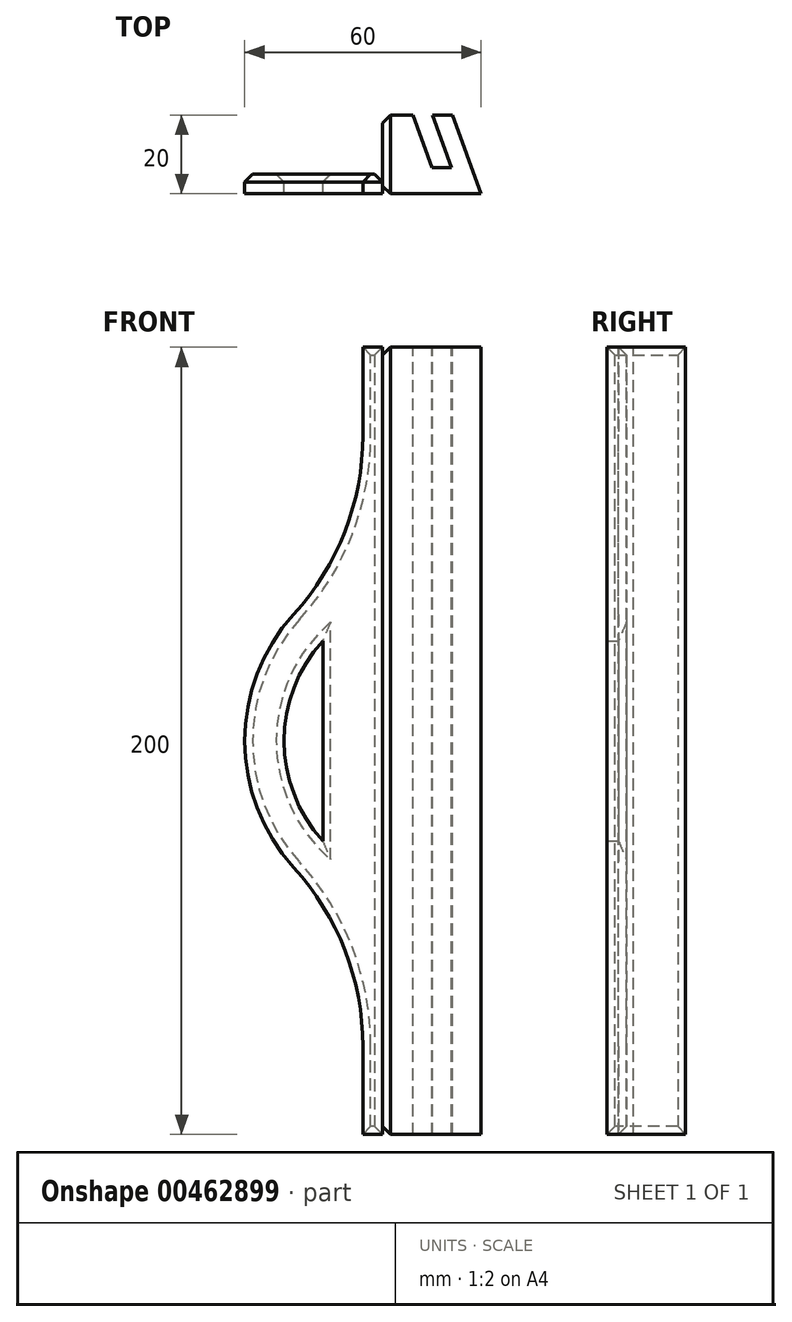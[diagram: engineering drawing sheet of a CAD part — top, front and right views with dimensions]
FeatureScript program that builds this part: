
annotation { "Feature Type Name" : "Feature", "Feature Type Description" : "" }
export const myFeature = defineFeature(function(context is Context, id is Id, definition is map)
    precondition{}
    {
        {
            var Q0;
            Q0=qCreatedBy(makeId("Top.planeOp"),FACE);
            var sketch = newSketch(context, id + "F0", { "sketchPlane" : qUnion([Q0])});
            skLineSegment(sketch, "E0", {"start": v(17.56, -12.97) * mm, "end": v(-7.44, -12.97) * mm});
            skLineSegment(sketch, "E1", {"start": v(-7.44, -12.97) * mm, "end": v(-0.16, 7.03) * mm});
            skLineSegment(sketch, "E2", {"start": v(-0.16, 7.03) * mm, "end": v(4.84, 7.03) * mm});
            skLineSegment(sketch, "E3", {"start": v(4.84, 7.03) * mm, "end": v(0, -6.27) * mm});
            skLineSegment(sketch, "E4", {"start": v(0, -6.27) * mm, "end": v(5, -6.27) * mm});
            skLineSegment(sketch, "E5", {"start": v(5, -6.27) * mm, "end": v(9.84, 7.03) * mm});
            skLineSegment(sketch, "E6", {"start": v(17.56, 7.03) * mm, "end": v(17.56, -12.97) * mm});
            skLineSegment(sketch, "E7", {"start": v(9.84, 7.03) * mm, "end": v(17.56, 7.03) * mm});
            skSolve(sketch);
        }
        {
            var Q0;
            Q0=qCreatedBy(makeId("Front.planeOp"),FACE);
            var sketch = newSketch(context, id + "F1", { "sketchPlane" : qUnion([Q0])});
            skLineSegment(sketch, "E8.left", {"start": v(0, 100) * mm, "end": v(0, 77.58) * mm});
            skArc(sketch, "E9", {"start": v(-17.57, 32.15) * mm, "mid": v(-30, 0) * mm, "end": v(-17.57, -32.15) * mm});
            skArc(sketch, "E10", {"start": v(0, -77.58) * mm, "mid": v(-4.54, -53.22) * mm, "end": v(-17.57, -32.15) * mm});
            skArc(sketch, "E11.trimOffspring", {"start": v(-17.57, 32.15) * mm, "mid": v(-4.54, 53.22) * mm, "end": v(0, 77.58) * mm});
            skArc(sketch, "E12.0", {"start": v(-10.17, 25.42) * mm, "mid": v(-20, 0) * mm, "end": v(-10.17, -25.42) * mm});
            skLineSegment(sketch, "E13", {"start": v(-10.17, 25.42) * mm, "end": v(-10.17, -25.42) * mm});
            skLineSegment(sketch, "E14", {"start": v(0, 100) * mm, "end": v(5, 100) * mm});
            skLineSegment(sketch, "E15", {"start": v(5, 100) * mm, "end": v(5, -100) * mm});
            skLineSegment(sketch, "E16", {"start": v(5, -100) * mm, "end": v(0, -100) * mm});
            skLineSegment(sketch, "E17.trimOffspring", {"start": v(0, -77.58) * mm, "end": v(0, -100) * mm});
            skSolve(sketch);
        }
        {
            var Q0;
            Q0=makeQuery(id+"F1.imprint","IMPRINT",FACE,{"disambiguationData":[TD([[makeQuery(id+"F1.imprint","IMPRINT",EDGE,{"derivedFrom":sQuery(id+"F1.wireOp",EDGE,"E8.left")}),1.0]])]});
            var Q1;
            Q1=sQuery(id+"F1.wireOp",EDGE,"E8.left");
            var Q2;
            Q2=sQuery(id+"F1.wireOp",EDGE,"E9");
            var Q3;
            Q3=sQuery(id+"F1.wireOp",EDGE,"E10");
            var Q4;
            Q4=sQuery(id+"F1.wireOp",EDGE,"E11.trimOffspring");
            var Q5;
            Q5=sQuery(id+"F1.wireOp",EDGE,"E15");
            var Q6;
            Q6=sQuery(id+"F1.wireOp",EDGE,"E17.trimOffspring");
            var Q7;
            Q7=sQuery(id+"F1.wireOp",EDGE,"E14");
            var Q8;
            Q8=sQuery(id+"F1.wireOp",EDGE,"E16");
            extrude(context, id + "F2", {"entities" : qUnion([Q0]), "surfaceEntities" : qUnion([Q1, Q2, Q3, Q4, Q5, Q6, Q7, Q8]), "depth" : 5 * mm});
        }
        {
            var Q0;
            Q0=makeQuery(id+"F0.imprint","IMPRINT",FACE,{"disambiguationData":[TD([[makeQuery(id+"F0.imprint","IMPRINT",EDGE,{"derivedFrom":sQuery(id+"F0.wireOp",EDGE,"E0")}),-1.0]])]});
            extrude(context, id + "F3", {"entities" : qUnion([Q0]), "depth" : 200 * mm});
        }
        {
            var Q0;
            Q0=makeQuery(id+"F3.opExtrude","SWEPT_BODY",BODY,{"disambiguationData":[OSD([sQuery(id+"F0.wireOp",EDGE,"E0"),sQuery(id+"F0.wireOp",EDGE,"E1"),sQuery(id+"F0.wireOp",EDGE,"E2"),sQuery(id+"F0.wireOp",EDGE,"E3"),sQuery(id+"F0.wireOp",EDGE,"E4"),sQuery(id+"F0.wireOp",EDGE,"E5"),sQuery(id+"F0.wireOp",EDGE,"E6"),sQuery(id+"F0.wireOp",EDGE,"E7")])]});
            var Q1;
            Q1=sQuery(id+"F0.wireOp",EDGE,"E6");
            transform(context, id + "F4", {"entities" : qUnion([Q0]), "transformType" : TransformType.ROTATION, "transformAxis" : qUnion([Q1]), "angle" : 180 * degree, "makeCopy" : false});
        }
        {
            var Q0;
            Q0=makeQuery(id+"F3.opExtrude","SWEPT_BODY",BODY,{"disambiguationData":[OSD([sQuery(id+"F0.wireOp",EDGE,"E0"),sQuery(id+"F0.wireOp",EDGE,"E1"),sQuery(id+"F0.wireOp",EDGE,"E2"),sQuery(id+"F0.wireOp",EDGE,"E3"),sQuery(id+"F0.wireOp",EDGE,"E4"),sQuery(id+"F0.wireOp",EDGE,"E5"),sQuery(id+"F0.wireOp",EDGE,"E6"),sQuery(id+"F0.wireOp",EDGE,"E7")])]});
            var Q1;
            Q1=makeQuery(id+"F3.opExtrude","CAP_VERTEX",VERTEX,{"disambiguationData":[OSD([sQuery(id+"F0.wireOp",EDGE,"E0"),sQuery(id+"F0.wireOp",EDGE,"E6")])],"isStart":false});
            var Q2;
            Q2=makeQuery(id+"F2.opExtrude","CAP_VERTEX",VERTEX,{"disambiguationData":[OSD([sQuery(id+"F1.wireOp",EDGE,"E15"),sQuery(id+"F1.wireOp",EDGE,"E16")])],"isStart":false});
            transform(context, id + "F5", {"entities" : qUnion([Q0]), "transformType" : TransformType.TRANSLATION_ENTITY, "oppositeDirectionEntity" : false, "transformLine" : qUnion([Q1, Q2]), "makeCopy" : false});
        }
        {
            var Q0;
            Q0=makeQuery(id+"F3.opExtrude","SWEPT_FACE",FACE,{"disambiguationData":[OSD([sQuery(id+"F0.wireOp",EDGE,"E6")])]});
            var Q1;
            Q1=makeQuery(id+"F2.opExtrude","CAP_FACE",FACE,{"disambiguationData":[OSD([sQuery(id+"F1.wireOp",EDGE,"E8.left"),sQuery(id+"F1.wireOp",EDGE,"E9"),sQuery(id+"F1.wireOp",EDGE,"E10"),sQuery(id+"F1.wireOp",EDGE,"E11.trimOffspring"),sQuery(id+"F1.wireOp",EDGE,"E12.0"),sQuery(id+"F1.wireOp",EDGE,"E13"),sQuery(id+"F1.wireOp",EDGE,"E14"),sQuery(id+"F1.wireOp",EDGE,"E15"),sQuery(id+"F1.wireOp",EDGE,"E16"),sQuery(id+"F1.wireOp",EDGE,"E17.trimOffspring")])],"isStart":true});
            chamfer(context, id + "F6", {"entities" : qUnion([Q0, Q1]), "width" : 2 * mm, "tangentPropagation" : true});
        }
    });
